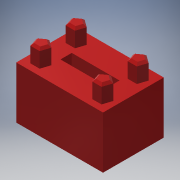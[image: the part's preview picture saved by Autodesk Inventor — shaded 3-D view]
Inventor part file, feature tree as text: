
AUTODESK INVENTOR PART (.ipt)
format: ipt  version: 2018.3 (Build 223284000, 284)  size: 225,280 bytes
history: native  units: mm
features: extrude x4, sketch x3, chamfer x2
ambient origin geometry x8: Origin, YZ Plane, XZ Plane, XY Plane, X Axis, Y Axis, Z Axis, Center Point
bodies: Solid1 (feature_tree)
feature tree (9):
  extrude  "Extrusion1"  Depth=14.0mm
  extrude  "Extrusion2"  Depth=12.0mm
  chamfer  "Chamfer1"  Distance=2.15mm
  extrude  "Extrusion3"  Depth=4.5mm
  chamfer  "Chamfer2"  Distance=4.0mm
  extrude  "Extrusion5"  Depth=4.5mm TaperAngle=45.0deg
  sketch  "Sketch1"  dims[d0=20.0mm d1=14.0mm]
  sketch  "Sketch3"  dims[d2=12.0mm d3=0.0mm d14=2.15mm d16=2.15mm d17=2.93mm]
  sketch  "Sketch5"  dims[d18=2.87mm d20=2.93mm d25=4.0mm d26=0.0mm d27=0.5mm d28=2.0mm d29=45.0deg d30=2.4mm d31=2.4mm d32=2.4mm d33=2.4mm d34=2.87mm d35=2.87mm d36=2.93mm d37=2.93mm d38=4.5mm d39=0.0mm d40=0.5mm d41=2.0mm d42=45.0deg d55=2.15mm d56=2.15mm d60=11.0mm d61=2.6mm d62=5.7mm d63=4.5mm d64=10.0mm d65=0.0mm]
